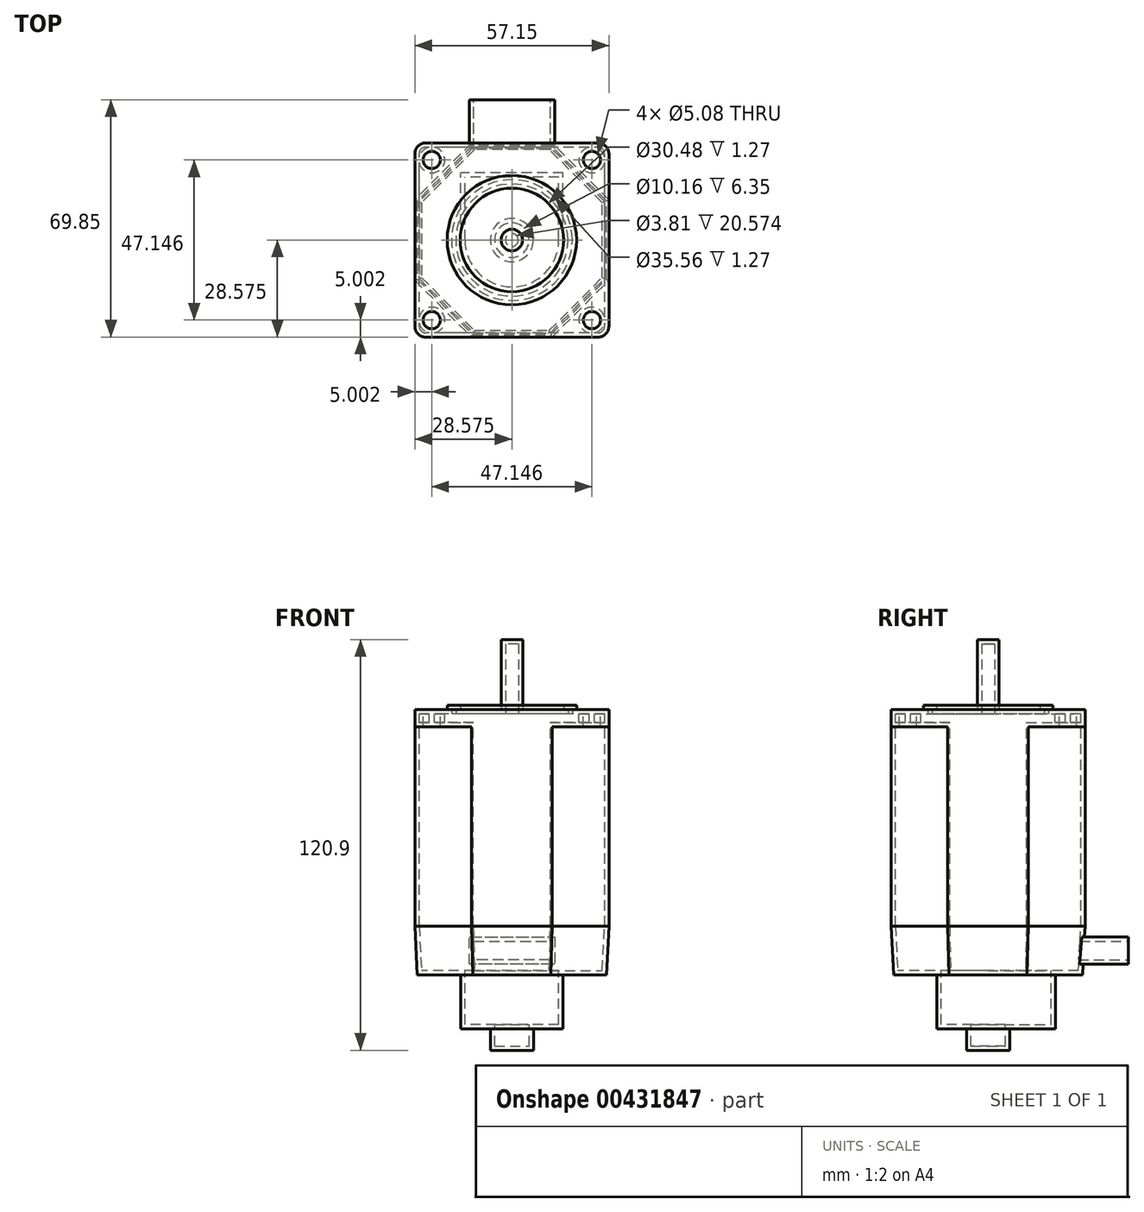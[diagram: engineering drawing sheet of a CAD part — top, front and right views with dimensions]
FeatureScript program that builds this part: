
annotation { "Feature Type Name" : "Feature", "Feature Type Description" : "" }
export const myFeature = defineFeature(function(context is Context, id is Id, definition is map)
    precondition{}
    {
        {
            var Q0;
            Q0=qCreatedBy(makeId("Top.planeOp"),FACE);
            var sketch = newSketch(context, id + "F0", { "sketchPlane" : qUnion([Q0])});
            skLineSegment(sketch, "E0.bottom", {"start": v(-3.17, 0) * mm, "end": v(-53.98, 0) * mm});
            skLineSegment(sketch, "E0.top", {"start": v(-3.18, 57.15) * mm, "end": v(-53.98, 57.15) * mm});
            skLineSegment(sketch, "E0.left", {"start": v(0, 3.17) * mm, "end": v(0, 53.98) * mm});
            skLineSegment(sketch, "E0.right", {"start": v(-57.15, 3.18) * mm, "end": v(-57.15, 53.98) * mm});
            skPoint(sketch, "E1.visualSharp", {"position": v(-57.15, 57.15) * mm});
            skArc(sketch, "E1.filletArc", {"start": v(-53.98, 57.15) * mm, "mid": v(-56.22, 56.22) * mm, "end": v(-57.15, 53.98) * mm});
            skPoint(sketch, "E2.visualSharp", {"position": v(0, 57.15) * mm});
            skArc(sketch, "E2.filletArc", {"start": v(0, 53.98) * mm, "mid": v(-0.93, 56.22) * mm, "end": v(-3.18, 57.15) * mm});
            skPoint(sketch, "E3.visualSharp", {"position": v(0, 0) * mm});
            skArc(sketch, "E3.filletArc", {"start": v(-3.17, 0) * mm, "mid": v(-0.93, 0.93) * mm, "end": v(0, 3.17) * mm});
            skPoint(sketch, "E4.visualSharp", {"position": v(-57.15, 0) * mm});
            skArc(sketch, "E4.filletArc", {"start": v(-57.15, 3.18) * mm, "mid": v(-56.22, 0.93) * mm, "end": v(-53.98, 0) * mm});
            skLineSegment(sketch, "E5", {"start": v(-28.58, 28.58) * mm, "end": v(-28.58, 99) * mm, "construction": true});
            skPoint(sketch, "E5.startSnap0", {"position": v(-57.15, 28.58) * mm});
            skPoint(sketch, "E5.startSnap1", {"position": v(-28.58, 57.15) * mm});
            skLineSegment(sketch, "E6", {"start": v(-28.58, 28.57) * mm, "end": v(23.41, 80.56) * mm, "construction": true});
            skCircle(sketch, "E7", {"center": v(-28.58, 28.58) * mm, "radius": 33.34 * mm, "construction": true});
            skCircle(sketch, "E8", {"center": v(-5, 52.15) * mm, "radius": 2.54 * mm});
            skCircle(sketch, "E9", {"center": v(-52.15, 52.15) * mm, "radius": 2.54 * mm});
            skCircle(sketch, "E10", {"center": v(-52.15, 5) * mm, "radius": 2.54 * mm});
            skCircle(sketch, "E11", {"center": v(-5, 5) * mm, "radius": 2.54 * mm});
            skCircle(sketch, "E12", {"center": v(-28.58, 28.58) * mm, "radius": 19.05 * mm});
            skCircle(sketch, "E13", {"center": v(-28.58, 28.57) * mm, "radius": 15.24 * mm});
            skCircle(sketch, "E14", {"center": v(-28.58, 28.58) * mm, "radius": 3.18 * mm});
            skSolve(sketch);
        }
        {
            var Q0;
            Q0=makeQuery(id+"F0.imprint","IMPRINT",FACE,{"disambiguationData":[TD([[makeQuery(id+"F0.imprint","IMPRINT",EDGE,{"derivedFrom":sQuery(id+"F0.wireOp",EDGE,"E0.bottom")}),-1.0]])]});
            var Q1;
            Q1=makeQuery(id+"F0.imprint","IMPRINT",FACE,{"disambiguationData":[TD([[makeQuery(id+"F0.imprint","IMPRINT",EDGE,{"derivedFrom":sQuery(id+"F0.wireOp",EDGE,"E12")}),1.0]])]});
            var Q2;
            Q2=makeQuery(id+"F0.imprint","IMPRINT",FACE,{"disambiguationData":[TD([[makeQuery(id+"F0.imprint","IMPRINT",EDGE,{"derivedFrom":sQuery(id+"F0.wireOp",EDGE,"E13")}),1.0]])]});
            var Q3;
            Q3=makeQuery(id+"F0.imprint","IMPRINT",FACE,{"disambiguationData":[TD([[makeQuery(id+"F0.imprint","IMPRINT",EDGE,{"derivedFrom":sQuery(id+"F0.wireOp",EDGE,"E14")}),1.0]])]});
            extrude(context, id + "F1", {"entities" : qUnion([Q0, Q1, Q2, Q3]), "oppositeDirection" : true, "depth" : 5.08 * mm});
        }
        {
            var Q0;
            Q0=makeQuery(id+"F0.imprint","IMPRINT",FACE,{"disambiguationData":[TD([[makeQuery(id+"F0.imprint","IMPRINT",EDGE,{"derivedFrom":sQuery(id+"F0.wireOp",EDGE,"E12")}),1.0]])]});
            extrude(context, id + "F2", {"entities" : qUnion([Q0]), "operationType" : NewBodyOperationType.ADD, "depth" : 1.27 * mm});
        }
        {
            var Q0;
            Q0=makeQuery(id+"F0.imprint","IMPRINT",FACE,{"disambiguationData":[TD([[makeQuery(id+"F0.imprint","IMPRINT",EDGE,{"derivedFrom":sQuery(id+"F0.wireOp",EDGE,"E14")}),1.0]])]});
            extrude(context, id + "F3", {"entities" : qUnion([Q0]), "operationType" : NewBodyOperationType.ADD, "depth" : 20.57 * mm});
        }
        {
            var Q0;
            Q0=makeQuery(id+"F1.opExtrude","CAP_FACE",FACE,{"disambiguationData":[OSD([sQuery(id+"F0.wireOp",EDGE,"E0.bottom"),sQuery(id+"F0.wireOp",EDGE,"E0.top"),sQuery(id+"F0.wireOp",EDGE,"E0.left"),sQuery(id+"F0.wireOp",EDGE,"E0.right"),sQuery(id+"F0.wireOp",EDGE,"E1.filletArc"),sQuery(id+"F0.wireOp",EDGE,"E2.filletArc"),sQuery(id+"F0.wireOp",EDGE,"E3.filletArc"),sQuery(id+"F0.wireOp",EDGE,"E4.filletArc"),sQuery(id+"F0.wireOp",EDGE,"E8"),sQuery(id+"F0.wireOp",EDGE,"E9"),sQuery(id+"F0.wireOp",EDGE,"E10"),sQuery(id+"F0.wireOp",EDGE,"E11"),sQuery(id+"F0.wireOp",EDGE,"E14")])],"isStart":false});
            var sketch = newSketch(context, id + "F4", { "sketchPlane" : qUnion([Q0])});
            skCircle(sketch, "E15.cCircle", {"center": v(-28.58, -28.58) * mm, "radius": 28.57 * mm, "construction": true});
            skLineSegment(sketch, "E15.0", {"start": v(-16.74, -57.15) * mm, "end": v(-40.41, -57.15) * mm});
            skLineSegment(sketch, "E15.1", {"start": v(-40.41, -57.15) * mm, "end": v(-57.15, -40.41) * mm});
            skLineSegment(sketch, "E15.2", {"start": v(-57.15, -40.41) * mm, "end": v(-57.15, -16.74) * mm});
            skLineSegment(sketch, "E15.3", {"start": v(-57.15, -16.74) * mm, "end": v(-40.41, 0) * mm});
            skLineSegment(sketch, "E15.4", {"start": v(-40.41, 0) * mm, "end": v(-16.74, 0) * mm});
            skLineSegment(sketch, "E15.5", {"start": v(-16.74, 0) * mm, "end": v(0, -16.74) * mm});
            skLineSegment(sketch, "E15.6", {"start": v(0, -16.74) * mm, "end": v(0, -40.41) * mm});
            skLineSegment(sketch, "E15.7", {"start": v(0, -40.41) * mm, "end": v(-16.74, -57.15) * mm});
            skPoint(sketch, "E15.0.midPoint", {"position": v(-28.58, -57.15) * mm});
            skLineSegment(sketch, "E16.0", {"start": v(-28.58, -28.57) * mm, "end": v(23.41, -80.56) * mm, "construction": true});
            skLineSegment(sketch, "E16.1", {"start": v(-28.58, -28.58) * mm, "end": v(-28.58, -99) * mm, "construction": true});
            skSolve(sketch);
        }
        {
            var Q0;
            Q0=makeQuery(id+"F4.imprint","IMPRINT",FACE,{"disambiguationData":[TD([[makeQuery(id+"F4.imprint","IMPRINT",EDGE,{"derivedFrom":sQuery(id+"F4.wireOp",EDGE,"E15.0")}),-1.0]])]});
            extrude(context, id + "F5", {"entities" : qUnion([Q0]), "operationType" : NewBodyOperationType.ADD, "depth" : 58.74 * mm});
        }
        {
            var Q0;
            Q0=makeQuery(id+"F5.opExtrude","CAP_FACE",FACE,{"disambiguationData":[OSD([sQuery(id+"F0.wireOp",EDGE,"E14"),sQuery(id+"F4.wireOp",EDGE,"E15.0"),sQuery(id+"F4.wireOp",EDGE,"E15.1"),sQuery(id+"F4.wireOp",EDGE,"E15.2"),sQuery(id+"F4.wireOp",EDGE,"E15.3"),sQuery(id+"F4.wireOp",EDGE,"E15.4"),sQuery(id+"F4.wireOp",EDGE,"E15.5"),sQuery(id+"F4.wireOp",EDGE,"E15.6"),sQuery(id+"F4.wireOp",EDGE,"E15.7")])],"isStart":false});
            extrude(context, id + "F6", {"entities" : qUnion([Q0]), "operationType" : NewBodyOperationType.ADD, "depth" : 14.29 * mm, "hasDraft" : true, "draftAngle" : 3 * degree, "draftPullDirection" : true});
        }
        {
            var Q0;
            Q0=makeQuery(id+"F6.opExtrude","CAP_FACE",FACE,{"disambiguationData":[OSD([sQuery(id+"F0.wireOp",EDGE,"E14"),sQuery(id+"F4.wireOp",EDGE,"E15.0"),sQuery(id+"F4.wireOp",EDGE,"E15.1"),sQuery(id+"F4.wireOp",EDGE,"E15.2"),sQuery(id+"F4.wireOp",EDGE,"E15.3"),sQuery(id+"F4.wireOp",EDGE,"E15.4"),sQuery(id+"F4.wireOp",EDGE,"E15.5"),sQuery(id+"F4.wireOp",EDGE,"E15.6"),sQuery(id+"F4.wireOp",EDGE,"E15.7")])],"isStart":false});
            var sketch = newSketch(context, id + "F7", { "sketchPlane" : qUnion([Q0])});
            skArc(sketch, "E17", {"start": v(-13.5, -28.58) * mm, "mid": v(-28.58, -13.5) * mm, "end": v(-43.66, -28.58) * mm});
            skCircle(sketch, "E18", {"center": v(-28.58, -28.58) * mm, "radius": 6.35 * mm});
            skLineSegment(sketch, "E19", {"start": v(-43.66, -28.58) * mm, "end": v(-43.66, -48.42) * mm});
            skLineSegment(sketch, "E20", {"start": v(-13.5, -28.58) * mm, "end": v(-13.5, -48.42) * mm});
            skLineSegment(sketch, "E21", {"start": v(-13.5, -48.42) * mm, "end": v(-43.66, -48.42) * mm});
            skLineSegment(sketch, "E22.0", {"start": v(-28.58, -28.58) * mm, "end": v(-28.58, -99) * mm, "construction": true});
            skLineSegment(sketch, "E22.1", {"start": v(-28.58, -28.57) * mm, "end": v(23.41, -80.56) * mm, "construction": true});
            skSolve(sketch);
        }
        {
            var Q0;
            Q0=makeQuery(id+"F7.imprint","IMPRINT",FACE,{"disambiguationData":[TD([[makeQuery(id+"F7.imprint","IMPRINT",EDGE,{"derivedFrom":sQuery(id+"F7.wireOp",EDGE,"E18")}),1.0]])]});
            extrude(context, id + "F8", {"entities" : qUnion([Q0]), "operationType" : NewBodyOperationType.ADD, "depth" : 22.22 * mm});
        }
        {
            var Q0;
            Q0=makeQuery(id+"F7.imprint","IMPRINT",FACE,{"disambiguationData":[TD([[makeQuery(id+"F7.imprint","IMPRINT",EDGE,{"derivedFrom":sQuery(id+"F7.wireOp",EDGE,"E17")}),1.0]])]});
            extrude(context, id + "F9", {"entities" : qUnion([Q0]), "operationType" : NewBodyOperationType.ADD, "depth" : 15.88 * mm});
        }
        {
            var Q0;
            Q0=makeQuery(id+"F5.boolean.opBoolean","MERGE",FACE,{"derivedFrom":[makeQuery(id+"F1.opExtrude","SWEPT_FACE",FACE,{"disambiguationData":[OSD([sQuery(id+"F0.wireOp",EDGE,"E0.top")])]}),makeQuery(id+"F5.opExtrude","SWEPT_FACE",FACE,{"disambiguationData":[OSD([sQuery(id+"F4.wireOp",EDGE,"E15.0")])]})]});
            var sketch = newSketch(context, id + "F10", { "sketchPlane" : qUnion([Q0])});
            skLineSegment(sketch, "E23.0", {"start": v(16.74, -63.82) * mm, "end": v(40.41, -63.82) * mm, "construction": true});
            skLineSegment(sketch, "E23.1", {"start": v(17.05, -78.1) * mm, "end": v(40.1, -78.1) * mm, "construction": true});
            skLineSegment(sketch, "E24", {"start": v(28.58, -78.1) * mm, "end": v(28.58, -63.82) * mm, "construction": true});
            skLineSegment(sketch, "E25", {"start": v(28.58, -74.93) * mm, "end": v(41.15, -74.93) * mm});
            skLineSegment(sketch, "E26", {"start": v(41.15, -74.93) * mm, "end": v(41.15, -67) * mm});
            skLineSegment(sketch, "E27", {"start": v(41.15, -67) * mm, "end": v(16, -67) * mm});
            skLineSegment(sketch, "E28", {"start": v(16, -67) * mm, "end": v(16, -74.93) * mm});
            skLineSegment(sketch, "E29", {"start": v(16, -74.93) * mm, "end": v(28.58, -74.93) * mm});
            skSolve(sketch);
        }
        {
            var Q0;
            Q0=makeQuery(id+"F10.imprint","IMPRINT",FACE,{"disambiguationData":[TD([[makeQuery(id+"F10.imprint","IMPRINT",EDGE,{"derivedFrom":sQuery(id+"F10.wireOp",EDGE,"E25")}),1.0]])]});
            extrude(context, id + "F11", {"entities" : qUnion([Q0]), "operationType" : NewBodyOperationType.ADD, "oppositeDirection" : true, "depth" : 3.17 * mm});
        }
        {
            var Q0;
            Q0=makeQuery(id+"F11.opExtrude","CAP_FACE",FACE,{"disambiguationData":[OSD([sQuery(id+"F10.wireOp",EDGE,"E25"),sQuery(id+"F10.wireOp",EDGE,"E26"),sQuery(id+"F10.wireOp",EDGE,"E27"),sQuery(id+"F10.wireOp",EDGE,"E28"),sQuery(id+"F10.wireOp",EDGE,"E29")])],"isStart":true});
            extrude(context, id + "F12", {"entities" : qUnion([Q0]), "operationType" : NewBodyOperationType.ADD, "depth" : 12.7 * mm});
        }
        {
            var Q0;
            Q0=makeQuery(id+"F12.opExtrude","CAP_FACE",FACE,{"disambiguationData":[OSD([sQuery(id+"F10.wireOp",EDGE,"E25"),sQuery(id+"F10.wireOp",EDGE,"E26"),sQuery(id+"F10.wireOp",EDGE,"E27"),sQuery(id+"F10.wireOp",EDGE,"E28"),sQuery(id+"F10.wireOp",EDGE,"E29")])],"isStart":false});
            shell(context, id + "F13", {"entities" : qUnion([Q0]), "thickness" : 1.27 * mm});
        }
    });
